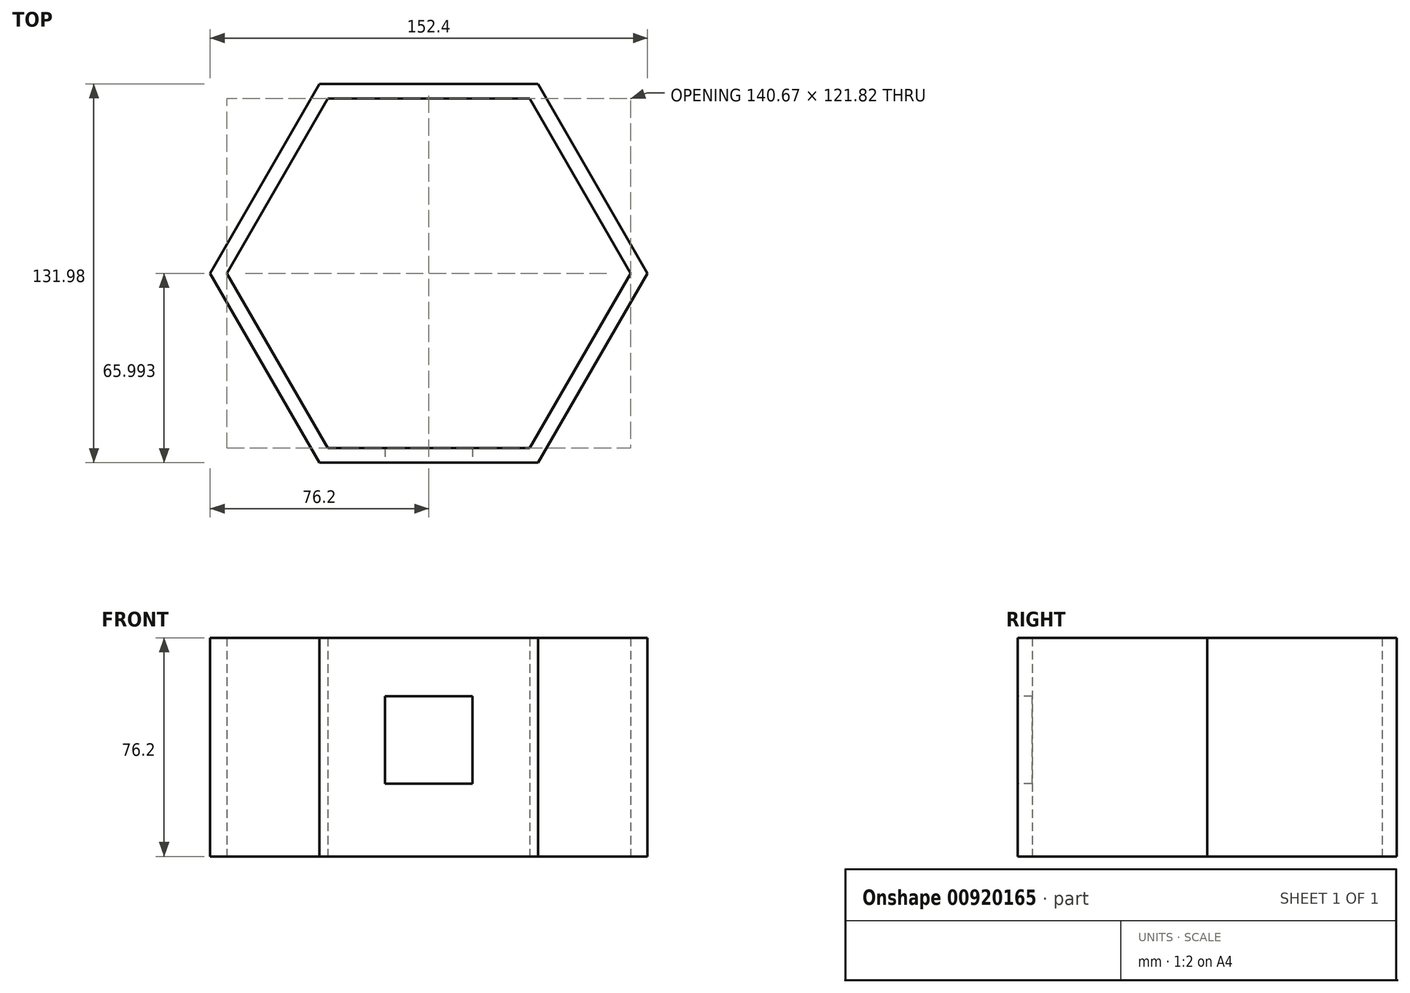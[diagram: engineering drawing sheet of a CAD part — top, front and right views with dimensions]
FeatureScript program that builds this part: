
annotation { "Feature Type Name" : "Feature", "Feature Type Description" : "" }
export const myFeature = defineFeature(function(context is Context, id is Id, definition is map)
    precondition{}
    {
        {
            var Q0;
            Q0=qCreatedBy(makeId("Top.planeOp"),FACE);
            var sketch = newSketch(context, id + "F0", { "sketchPlane" : qUnion([Q0])});
            skLineSegment(sketch, "E0", {"start": v(-68.42, 21.8) * mm, "end": v(-30.32, 87.8) * mm});
            skLineSegment(sketch, "E1", {"start": v(-30.32, 87.8) * mm, "end": v(45.88, 87.8) * mm});
            skLineSegment(sketch, "E2", {"start": v(45.88, 87.8) * mm, "end": v(83.98, 21.8) * mm});
            skLineSegment(sketch, "E3", {"start": v(83.98, 21.8) * mm, "end": v(45.88, -44.19) * mm});
            skLineSegment(sketch, "E4", {"start": v(45.88, -44.19) * mm, "end": v(-30.32, -44.19) * mm});
            skLineSegment(sketch, "E5", {"start": v(-30.32, -44.19) * mm, "end": v(-68.42, 21.8) * mm});
            skLineSegment(sketch, "E6", {"start": v(-30.32, 87.8) * mm, "end": v(-30.32, -56.74) * mm, "construction": true});
            skLineSegment(sketch, "E7", {"start": v(-68.42, 21.8) * mm, "end": v(102.94, -77.13) * mm, "construction": true});
            skLineSegment(sketch, "E8.0", {"start": v(-62.55, 21.8) * mm, "end": v(-27.39, 82.71) * mm});
            skLineSegment(sketch, "E9.0", {"start": v(-27.39, 82.71) * mm, "end": v(42.95, 82.71) * mm});
            skLineSegment(sketch, "E10.0", {"start": v(42.95, 82.71) * mm, "end": v(78.11, 21.8) * mm});
            skLineSegment(sketch, "E11.0", {"start": v(78.11, 21.8) * mm, "end": v(42.95, -39.1) * mm});
            skLineSegment(sketch, "E12.0", {"start": v(42.95, -39.1) * mm, "end": v(-27.39, -39.1) * mm});
            skLineSegment(sketch, "E13.0", {"start": v(-27.39, -39.1) * mm, "end": v(-62.55, 21.8) * mm});
            skLineSegment(sketch, "E14.top", {"start": v(-7.85, -39.1) * mm, "end": v(42.95, -39.1) * mm});
            skSolve(sketch);
        }
        {
            var Q0;
            Q0=qCreatedBy(makeId("Top.planeOp"),FACE);
            var sketch = newSketch(context, id + "F1", { "sketchPlane" : qUnion([Q0])});
            skLineSegment(sketch, "E15", {"start": v(-22.7, 21.8) * mm, "end": v(-7.46, 48.2) * mm});
            skLineSegment(sketch, "E16", {"start": v(-7.46, 48.2) * mm, "end": v(23.02, 48.2) * mm});
            skLineSegment(sketch, "E17", {"start": v(23.02, 48.2) * mm, "end": v(38.26, 21.8) * mm});
            skLineSegment(sketch, "E18", {"start": v(38.26, 21.8) * mm, "end": v(23.02, -4.6) * mm});
            skLineSegment(sketch, "E19", {"start": v(23.02, -4.6) * mm, "end": v(-7.46, -4.6) * mm});
            skLineSegment(sketch, "E20", {"start": v(-7.46, -4.6) * mm, "end": v(-22.7, 21.8) * mm});
            skLineSegment(sketch, "E21", {"start": v(-7.46, 48.2) * mm, "end": v(-27.39, 82.71) * mm, "construction": true});
            skLineSegment(sketch, "E22", {"start": v(23.02, -4.6) * mm, "end": v(42.95, -39.1) * mm, "construction": true});
            skLineSegment(sketch, "E23", {"start": v(-22.7, 21.8) * mm, "end": v(-62.55, 21.8) * mm, "construction": true});
            skLineSegment(sketch, "E24", {"start": v(38.26, 21.8) * mm, "end": v(78.11, 21.8) * mm, "construction": true});
            skLineSegment(sketch, "E25", {"start": v(23.02, 48.2) * mm, "end": v(42.95, 82.71) * mm, "construction": true});
            skLineSegment(sketch, "E26", {"start": v(-7.46, -4.6) * mm, "end": v(-27.39, -39.1) * mm, "construction": true});
            skLineSegment(sketch, "E27.0", {"start": v(-4.53, 0.49) * mm, "end": v(-16.83, 21.8) * mm});
            skLineSegment(sketch, "E27.1", {"start": v(-4.53, 43.12) * mm, "end": v(20.09, 43.12) * mm});
            skLineSegment(sketch, "E27.2", {"start": v(20.09, 43.12) * mm, "end": v(32.4, 21.8) * mm});
            skLineSegment(sketch, "E27.3", {"start": v(-16.83, 21.8) * mm, "end": v(-4.53, 43.12) * mm});
            skLineSegment(sketch, "E27.4", {"start": v(32.4, 21.8) * mm, "end": v(20.09, 0.49) * mm});
            skLineSegment(sketch, "E27.5", {"start": v(20.09, 0.49) * mm, "end": v(-4.53, 0.49) * mm});
            skSolve(sketch);
        }
        {
            var Q0;
            Q0=makeQuery(id+"F0.imprint","IMPRINT",FACE,{"disambiguationData":[TD([[makeQuery(id+"F0.imprint","IMPRINT",EDGE,{"derivedFrom":sQuery(id+"F0.wireOp",EDGE,"E0")}),-1.0]])]});
            extrude(context, id + "F2", {"entities" : qUnion([Q0]), "depth" : 76.2 * mm, "offsetDistance" : 25.4 * mm});
        }
        {
            var Q0;
            Q0=makeQuery(id+"F2.opExtrude","SWEPT_FACE",FACE,{"disambiguationData":[OSD([sQuery(id+"F0.wireOp",EDGE,"E4")])]});
            var sketch = newSketch(context, id + "F3", { "sketchPlane" : qUnion([Q0])});
            skLineSegment(sketch, "E28", {"start": v(-30.32, 25.4) * mm, "end": v(45.88, 25.4) * mm, "construction": true});
            skLineSegment(sketch, "E29.bottom", {"start": v(-7.46, 25.4) * mm, "end": v(23.02, 25.4) * mm});
            skLineSegment(sketch, "E29.top", {"start": v(-7.46, 55.88) * mm, "end": v(23.02, 55.88) * mm});
            skLineSegment(sketch, "E29.left", {"start": v(-7.46, 25.4) * mm, "end": v(-7.46, 55.88) * mm});
            skLineSegment(sketch, "E29.right", {"start": v(23.02, 25.4) * mm, "end": v(23.02, 55.88) * mm});
            skSolve(sketch);
        }
        {
            var Q0;
            Q0=makeQuery(id+"F3.imprint","IMPRINT",FACE,{"disambiguationData":[TD([[makeQuery(id+"F3.imprint","IMPRINT",EDGE,{"derivedFrom":sQuery(id+"F3.wireOp",EDGE,"E29.bottom")}),1.0]])]});
            extrude(context, id + "F4", {"entities" : qUnion([Q0]), "operationType" : NewBodyOperationType.REMOVE, "oppositeDirection" : true, "depth" : 5.08 * mm, "offsetDistance" : 25.4 * mm});
        }
    });
